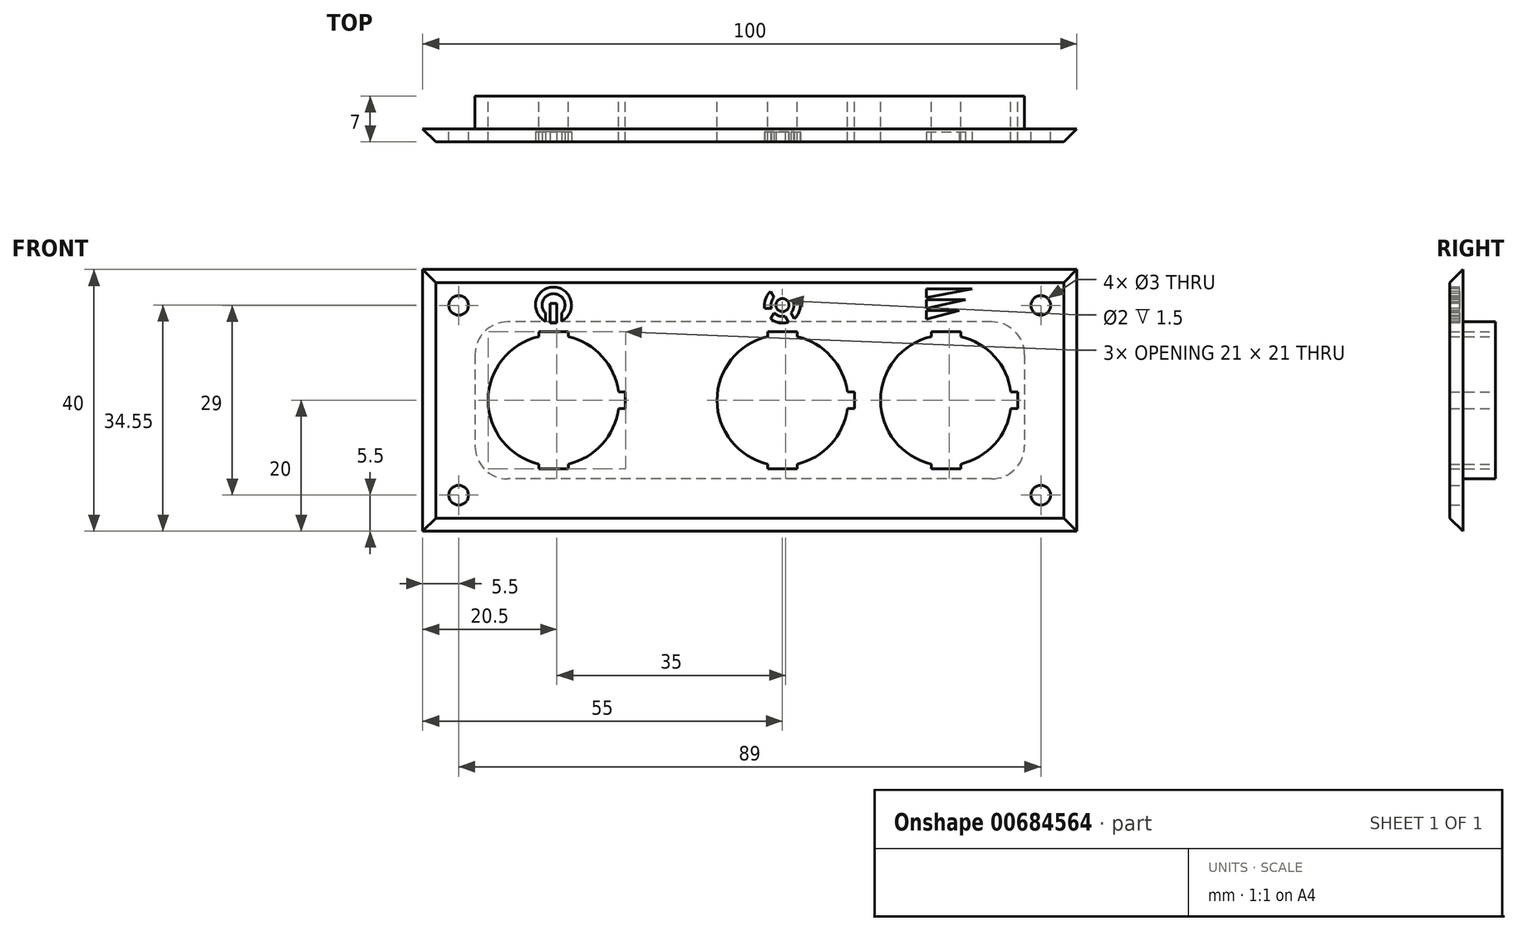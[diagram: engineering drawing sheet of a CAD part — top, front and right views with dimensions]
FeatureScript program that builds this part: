
annotation { "Feature Type Name" : "Feature", "Feature Type Description" : "" }
export const myFeature = defineFeature(function(context is Context, id is Id, definition is map)
    precondition{}
    {
        {
            var Q0;
            Q0=qCreatedBy(makeId("Front.planeOp"),FACE);
            var sketch = newSketch(context, id + "F0", { "sketchPlane" : qUnion([Q0])});
            skLineSegment(sketch, "E0.bottom", {"start": v(0, 0) * mm, "end": v(100, 0) * mm});
            skLineSegment(sketch, "E0.top", {"start": v(0, 40) * mm, "end": v(100, 40) * mm});
            skLineSegment(sketch, "E0.left", {"start": v(0, 0) * mm, "end": v(0, 40) * mm});
            skLineSegment(sketch, "E0.right", {"start": v(100, 0) * mm, "end": v(100, 40) * mm});
            skSolve(sketch);
        }
        {
            var Q0;
            Q0=makeQuery(id+"F0.imprint","IMPRINT",FACE,{"disambiguationData":[TD([[makeQuery(id+"F0.imprint","IMPRINT",EDGE,{"derivedFrom":sQuery(id+"F0.wireOp",EDGE,"E0.bottom")}),1.0]])]});
            extrude(context, id + "F1", {"entities" : qUnion([Q0]), "depth" : 2 * mm});
        }
        {
            var Q0;
            Q0=makeQuery(id+"F1.opExtrude","CAP_EDGE",EDGE,{"disambiguationData":[OSD([sQuery(id+"F0.wireOp",EDGE,"E0.right")])],"isStart":false});
            var Q1;
            Q1=makeQuery(id+"F1.opExtrude","CAP_EDGE",EDGE,{"disambiguationData":[OSD([sQuery(id+"F0.wireOp",EDGE,"E0.top")])],"isStart":false});
            var Q2;
            Q2=makeQuery(id+"F1.opExtrude","CAP_EDGE",EDGE,{"disambiguationData":[OSD([sQuery(id+"F0.wireOp",EDGE,"E0.bottom")])],"isStart":false});
            var Q3;
            Q3=makeQuery(id+"F1.opExtrude","CAP_EDGE",EDGE,{"disambiguationData":[OSD([sQuery(id+"F0.wireOp",EDGE,"E0.left")])],"isStart":false});
            chamfer(context, id + "F2", {"entities" : qUnion([Q0, Q1, Q2, Q3]), "width" : 2 * mm, "tangentPropagation" : true});
        }
        {
            var Q0;
            Q0=makeQuery(id+"F1.opExtrude","CAP_FACE",FACE,{"disambiguationData":[OSD([sQuery(id+"F0.wireOp",EDGE,"E0.bottom"),sQuery(id+"F0.wireOp",EDGE,"E0.top"),sQuery(id+"F0.wireOp",EDGE,"E0.left"),sQuery(id+"F0.wireOp",EDGE,"E0.right")])],"isStart":true});
            var sketch = newSketch(context, id + "F3", { "sketchPlane" : qUnion([Q0])});
            skLineSegment(sketch, "E1.bottom", {"start": v(-92, 32) * mm, "end": v(-8, 32) * mm});
            skLineSegment(sketch, "E1.top", {"start": v(-92, 8) * mm, "end": v(-8, 8) * mm});
            skLineSegment(sketch, "E1.left", {"start": v(-92, 32) * mm, "end": v(-92, 8) * mm});
            skLineSegment(sketch, "E1.right", {"start": v(-8, 32) * mm, "end": v(-8, 8) * mm});
            skSolve(sketch);
        }
        {
            var Q0;
            Q0=makeQuery(id+"F3.imprint","IMPRINT",FACE,{"disambiguationData":[TD([[makeQuery(id+"F3.imprint","IMPRINT",EDGE,{"derivedFrom":sQuery(id+"F3.wireOp",EDGE,"E1.bottom")}),-1.0]])]});
            extrude(context, id + "F4", {"entities" : qUnion([Q0]), "operationType" : NewBodyOperationType.ADD, "depth" : 5 * mm});
        }
        {
            var Q0;
            Q0=makeQuery(id+"F1.opExtrude","CAP_FACE",FACE,{"disambiguationData":[OSD([sQuery(id+"F0.wireOp",EDGE,"E0.bottom"),sQuery(id+"F0.wireOp",EDGE,"E0.top"),sQuery(id+"F0.wireOp",EDGE,"E0.left"),sQuery(id+"F0.wireOp",EDGE,"E0.right")])],"isStart":true});
            var sketch = newSketch(context, id + "F5", { "sketchPlane" : qUnion([Q0])});
            skCircle(sketch, "E2", {"center": v(-94.5, 34.5) * mm, "radius": 1.5 * mm});
            skCircle(sketch, "E3", {"center": v(-5.5, 34.5) * mm, "radius": 1.5 * mm});
            skCircle(sketch, "E4", {"center": v(-5.5, 5.5) * mm, "radius": 1.5 * mm});
            skCircle(sketch, "E5", {"center": v(-94.5, 5.5) * mm, "radius": 1.5 * mm});
            skSolve(sketch);
        }
        {
            var Q0;
            Q0=makeQuery(id+"F5.imprint","IMPRINT",FACE,{"disambiguationData":[TD([[makeQuery(id+"F5.imprint","IMPRINT",EDGE,{"derivedFrom":sQuery(id+"F5.wireOp",EDGE,"E2")}),1.0]])]});
            var Q1;
            Q1=makeQuery(id+"F5.imprint","IMPRINT",FACE,{"disambiguationData":[TD([[makeQuery(id+"F5.imprint","IMPRINT",EDGE,{"derivedFrom":sQuery(id+"F5.wireOp",EDGE,"E5")}),1.0]])]});
            var Q2;
            Q2=makeQuery(id+"F5.imprint","IMPRINT",FACE,{"disambiguationData":[TD([[makeQuery(id+"F5.imprint","IMPRINT",EDGE,{"derivedFrom":sQuery(id+"F5.wireOp",EDGE,"E3")}),1.0]])]});
            var Q3;
            Q3=makeQuery(id+"F5.imprint","IMPRINT",FACE,{"disambiguationData":[TD([[makeQuery(id+"F5.imprint","IMPRINT",EDGE,{"derivedFrom":sQuery(id+"F5.wireOp",EDGE,"E4")}),1.0]])]});
            extrude(context, id + "F6", {"entities" : qUnion([Q0, Q1, Q2, Q3]), "operationType" : NewBodyOperationType.REMOVE, "endBound" : BoundingType.THROUGH_ALL, "oppositeDirection" : true, "depth" : 25 * mm});
        }
        {
            var Q0;
            Q0=makeQuery(id+"F4.opExtrude","SWEPT_EDGE",EDGE,{"disambiguationData":[OSD([sQuery(id+"F3.wireOp",EDGE,"E1.top"),sQuery(id+"F3.wireOp",EDGE,"E1.left")])]});
            var Q1;
            Q1=makeQuery(id+"F4.opExtrude","SWEPT_EDGE",EDGE,{"disambiguationData":[OSD([sQuery(id+"F3.wireOp",EDGE,"E1.bottom"),sQuery(id+"F3.wireOp",EDGE,"E1.left")])]});
            var Q2;
            Q2=makeQuery(id+"F4.opExtrude","SWEPT_EDGE",EDGE,{"disambiguationData":[OSD([sQuery(id+"F3.wireOp",EDGE,"E1.top"),sQuery(id+"F3.wireOp",EDGE,"E1.right")])]});
            var Q3;
            Q3=makeQuery(id+"F4.opExtrude","SWEPT_EDGE",EDGE,{"disambiguationData":[OSD([sQuery(id+"F3.wireOp",EDGE,"E1.bottom"),sQuery(id+"F3.wireOp",EDGE,"E1.right")])]});
            fillet(context, id + "F7", {"entities" : qUnion([Q0, Q1, Q2, Q3]), "radius" : 5 * mm, "tangentPropagation" : true, "allowEdgeOverflow" : false});
        }
        {
            var Q0;
            Q0=makeQuery(id+"F4.opExtrude","CAP_FACE",FACE,{"disambiguationData":[OSD([sQuery(id+"F3.wireOp",EDGE,"E1.bottom"),sQuery(id+"F3.wireOp",EDGE,"E1.top"),sQuery(id+"F3.wireOp",EDGE,"E1.left"),sQuery(id+"F3.wireOp",EDGE,"E1.right")])],"isStart":false});
            var sketch = newSketch(context, id + "F8", { "sketchPlane" : qUnion([Q0])});
            skCircle(sketch, "E6", {"center": v(-80, 20) * mm, "radius": 10 * mm});
            skCircle(sketch, "E7", {"center": v(-55, 20) * mm, "radius": 10 * mm});
            skCircle(sketch, "E8", {"center": v(-20, 20) * mm, "radius": 10 * mm});
            skSolve(sketch);
        }
        {
            var Q0;
            Q0=makeQuery(id+"F8.imprint","IMPRINT",FACE,{"disambiguationData":[TD([[makeQuery(id+"F8.imprint","IMPRINT",EDGE,{"derivedFrom":sQuery(id+"F8.wireOp",EDGE,"E6")}),1.0]])]});
            var Q1;
            Q1=makeQuery(id+"F8.imprint","IMPRINT",FACE,{"disambiguationData":[TD([[makeQuery(id+"F8.imprint","IMPRINT",EDGE,{"derivedFrom":sQuery(id+"F8.wireOp",EDGE,"E7")}),1.0]])]});
            var Q2;
            Q2=makeQuery(id+"F8.imprint","IMPRINT",FACE,{"disambiguationData":[TD([[makeQuery(id+"F8.imprint","IMPRINT",EDGE,{"derivedFrom":sQuery(id+"F8.wireOp",EDGE,"E8")}),1.0]])]});
            extrude(context, id + "F9", {"entities" : qUnion([Q0, Q1, Q2]), "operationType" : NewBodyOperationType.REMOVE, "endBound" : BoundingType.THROUGH_ALL, "oppositeDirection" : true, "depth" : 25 * mm});
        }
        {
            var Q0;
            Q0=makeQuery(id+"F4.opExtrude","CAP_FACE",FACE,{"disambiguationData":[OSD([sQuery(id+"F3.wireOp",EDGE,"E1.bottom"),sQuery(id+"F3.wireOp",EDGE,"E1.top"),sQuery(id+"F3.wireOp",EDGE,"E1.left"),sQuery(id+"F3.wireOp",EDGE,"E1.right")])],"isStart":false});
            var sketch = newSketch(context, id + "F10", { "sketchPlane" : qUnion([Q0])});
            skLineSegment(sketch, "E9.bottom", {"start": v(-91, 21.25) * mm, "end": v(-85.88, 21.25) * mm});
            skLineSegment(sketch, "E9.top", {"start": v(-91, 18.75) * mm, "end": v(-85.88, 18.75) * mm});
            skLineSegment(sketch, "E9.left", {"start": v(-91, 21.25) * mm, "end": v(-91, 18.75) * mm});
            skLineSegment(sketch, "E9.right", {"start": v(-85.88, 21.25) * mm, "end": v(-85.88, 18.75) * mm});
            skLineSegment(sketch, "E10.bottom", {"start": v(-66, 21.25) * mm, "end": v(-50.9, 21.25) * mm});
            skLineSegment(sketch, "E10.top", {"start": v(-66, 18.75) * mm, "end": v(-50.9, 18.75) * mm});
            skLineSegment(sketch, "E10.left", {"start": v(-66, 21.25) * mm, "end": v(-66, 18.75) * mm});
            skLineSegment(sketch, "E10.right", {"start": v(-50.9, 21.25) * mm, "end": v(-50.9, 18.75) * mm});
            skLineSegment(sketch, "E11.bottom", {"start": v(-31, 21.25) * mm, "end": v(-25.22, 21.25) * mm});
            skLineSegment(sketch, "E11.top", {"start": v(-31, 18.75) * mm, "end": v(-25.22, 18.75) * mm});
            skLineSegment(sketch, "E11.left", {"start": v(-31, 21.25) * mm, "end": v(-31, 18.75) * mm});
            skLineSegment(sketch, "E11.right", {"start": v(-25.22, 21.25) * mm, "end": v(-25.22, 18.75) * mm});
            skSolve(sketch);
        }
        {
            var Q0;
            {var subQ0=sQuery(id+"F10.wireOp",EDGE,"E9.left");Q0=makeQuery(id+"F10.imprint","IMPRINT",FACE,{"disambiguationData":[TD([[makeQuery(id+"F10.imprint","IMPRINT",EDGE,{"derivedFrom":subQ0}),1.0]])]});}
            var Q1;
            {var subQ0=sQuery(id+"F10.wireOp",EDGE,"E10.left");Q1=makeQuery(id+"F10.imprint","IMPRINT",FACE,{"disambiguationData":[TD([[makeQuery(id+"F10.imprint","IMPRINT",EDGE,{"derivedFrom":subQ0}),1.0]])]});}
            var Q2;
            {var subQ0=sQuery(id+"F10.wireOp",EDGE,"E11.left");Q2=makeQuery(id+"F10.imprint","IMPRINT",FACE,{"disambiguationData":[TD([[makeQuery(id+"F10.imprint","IMPRINT",EDGE,{"derivedFrom":subQ0}),1.0]])]});}
            extrude(context, id + "F11", {"entities" : qUnion([Q0, Q1, Q2]), "operationType" : NewBodyOperationType.REMOVE, "endBound" : BoundingType.THROUGH_ALL, "oppositeDirection" : true, "depth" : 5 * mm});
        }
        {
            var Q0;
            Q0=makeQuery(id+"F4.opExtrude","CAP_FACE",FACE,{"disambiguationData":[OSD([sQuery(id+"F3.wireOp",EDGE,"E1.bottom"),sQuery(id+"F3.wireOp",EDGE,"E1.top"),sQuery(id+"F3.wireOp",EDGE,"E1.left"),sQuery(id+"F3.wireOp",EDGE,"E1.right")])],"isStart":false});
            var sketch = newSketch(context, id + "F12", { "sketchPlane" : qUnion([Q0])});
            skLineSegment(sketch, "E12.bottom", {"start": v(-82.25, 30.5) * mm, "end": v(-77.75, 30.5) * mm});
            skLineSegment(sketch, "E12.top", {"start": v(-82.25, 9.5) * mm, "end": v(-77.75, 9.5) * mm});
            skLineSegment(sketch, "E12.left", {"start": v(-82.25, 30.5) * mm, "end": v(-82.25, 9.5) * mm});
            skLineSegment(sketch, "E12.right", {"start": v(-77.75, 30.5) * mm, "end": v(-77.75, 9.5) * mm});
            skLineSegment(sketch, "E13.bottom", {"start": v(-57.25, 30.5) * mm, "end": v(-52.75, 30.5) * mm});
            skLineSegment(sketch, "E13.top", {"start": v(-57.25, 9.5) * mm, "end": v(-52.75, 9.5) * mm});
            skLineSegment(sketch, "E13.left", {"start": v(-57.25, 30.5) * mm, "end": v(-57.25, 9.5) * mm});
            skLineSegment(sketch, "E13.right", {"start": v(-52.75, 30.5) * mm, "end": v(-52.75, 9.5) * mm});
            skLineSegment(sketch, "E14.bottom", {"start": v(-22.25, 30.5) * mm, "end": v(-17.75, 30.5) * mm});
            skLineSegment(sketch, "E14.top", {"start": v(-22.25, 9.5) * mm, "end": v(-17.75, 9.5) * mm});
            skLineSegment(sketch, "E14.left", {"start": v(-22.25, 30.5) * mm, "end": v(-22.25, 9.5) * mm});
            skLineSegment(sketch, "E14.right", {"start": v(-17.75, 30.5) * mm, "end": v(-17.75, 9.5) * mm});
            skSolve(sketch);
        }
        {
            var Q0;
            {var subQ0=sQuery(id+"F12.wireOp",EDGE,"E12.bottom");Q0=makeQuery(id+"F12.imprint","IMPRINT",FACE,{"disambiguationData":[TD([[makeQuery(id+"F12.imprint","IMPRINT",EDGE,{"derivedFrom":subQ0}),-1.0]])]});}
            var Q1;
            {var subQ0=sQuery(id+"F12.wireOp",EDGE,"E12.top");Q1=makeQuery(id+"F12.imprint","IMPRINT",FACE,{"disambiguationData":[TD([[makeQuery(id+"F12.imprint","IMPRINT",EDGE,{"derivedFrom":subQ0}),1.0]])]});}
            var Q2;
            {var subQ0=sQuery(id+"F12.wireOp",EDGE,"E13.top");Q2=makeQuery(id+"F12.imprint","IMPRINT",FACE,{"disambiguationData":[TD([[makeQuery(id+"F12.imprint","IMPRINT",EDGE,{"derivedFrom":subQ0}),1.0]])]});}
            var Q3;
            {var subQ0=sQuery(id+"F12.wireOp",EDGE,"E13.bottom");Q3=makeQuery(id+"F12.imprint","IMPRINT",FACE,{"disambiguationData":[TD([[makeQuery(id+"F12.imprint","IMPRINT",EDGE,{"derivedFrom":subQ0}),-1.0]])]});}
            var Q4;
            {var subQ0=sQuery(id+"F12.wireOp",EDGE,"E14.bottom");Q4=makeQuery(id+"F12.imprint","IMPRINT",FACE,{"disambiguationData":[TD([[makeQuery(id+"F12.imprint","IMPRINT",EDGE,{"derivedFrom":subQ0}),-1.0]])]});}
            var Q5;
            {var subQ0=sQuery(id+"F12.wireOp",EDGE,"E14.top");Q5=makeQuery(id+"F12.imprint","IMPRINT",FACE,{"disambiguationData":[TD([[makeQuery(id+"F12.imprint","IMPRINT",EDGE,{"derivedFrom":subQ0}),1.0]])]});}
            extrude(context, id + "F13", {"entities" : qUnion([Q0, Q1, Q2, Q3, Q4, Q5]), "operationType" : NewBodyOperationType.REMOVE, "endBound" : BoundingType.THROUGH_ALL, "oppositeDirection" : true, "depth" : 5.5 * mm});
        }
        {
            var Q0;
            Q0=makeQuery(id+"F1.opExtrude","CAP_FACE",FACE,{"disambiguationData":[OSD([sQuery(id+"F0.wireOp",EDGE,"E0.bottom"),sQuery(id+"F0.wireOp",EDGE,"E0.top"),sQuery(id+"F0.wireOp",EDGE,"E0.left"),sQuery(id+"F0.wireOp",EDGE,"E0.right")])],"isStart":false});
            var sketch = newSketch(context, id + "F14", { "sketchPlane" : qUnion([Q0])});
            skLineSegment(sketch, "E15", {"start": v(2.8, 37.3) * mm, "end": v(102.8, 37.3) * mm, "construction": true});
            skLineSegment(sketch, "E16", {"start": v(3.28, 31.8) * mm, "end": v(103.18, 31.8) * mm, "construction": true});
            skLineSegment(sketch, "E17.bottom", {"start": v(19.5, 31.8) * mm, "end": v(20.5, 31.8) * mm});
            skLineSegment(sketch, "E17.top", {"start": v(19.5, 34.8) * mm, "end": v(20.5, 34.8) * mm});
            skLineSegment(sketch, "E17.left", {"start": v(19.5, 31.8) * mm, "end": v(19.5, 34.8) * mm});
            skLineSegment(sketch, "E17.right", {"start": v(20.5, 31.8) * mm, "end": v(20.5, 34.8) * mm});
            skCircle(sketch, "E18", {"center": v(20, 34.55) * mm, "radius": 2.75 * mm});
            skCircle(sketch, "E19", {"center": v(20, 34.55) * mm, "radius": 1.75 * mm});
            skLineSegment(sketch, "E20.bottom", {"start": v(18.75, 30.98) * mm, "end": v(21.25, 30.98) * mm});
            skLineSegment(sketch, "E20.top", {"start": v(18.75, 35.15) * mm, "end": v(21.25, 35.15) * mm});
            skLineSegment(sketch, "E20.left", {"start": v(18.75, 30.98) * mm, "end": v(18.75, 35.15) * mm});
            skLineSegment(sketch, "E20.right", {"start": v(21.25, 30.98) * mm, "end": v(21.25, 35.15) * mm});
            skSolve(sketch);
        }
        {
            var Q0;
            {var subQ0=sQuery(id+"F14.wireOp",EDGE,"E20.left");var subQ1=sQuery(id+"F14.wireOp",EDGE,"E18");var subQ2=makeQuery(id+"F14.imprint","INTERSECT",VERTEX,{"derivedFrom":[subQ1,subQ0]});Q0=makeQuery(id+"F14.imprint","IMPRINT",FACE,{"disambiguationData":[TD([[makeQuery(id+"F14.imprint","IMPRINT",EDGE,{"disambiguationData":[TD([[subQ2,1.0]])],"derivedFrom":subQ1}),1.0]])]});}
            var Q1;
            {var subQ0=sQuery(id+"F14.wireOp",EDGE,"E17.top");Q1=makeQuery(id+"F14.imprint","IMPRINT",FACE,{"disambiguationData":[TD([[makeQuery(id+"F14.imprint","IMPRINT",EDGE,{"derivedFrom":subQ0}),-1.0]])]});}
            var Q2;
            {var subQ0=sQuery(id+"F14.wireOp",EDGE,"E18");var subQ4=sQuery(id+"F14.wireOp",EDGE,"E17.left");var subQ5=makeQuery(id+"F14.imprint","INTERSECT",VERTEX,{"derivedFrom":[subQ4,subQ0]});Q2=makeQuery(id+"F14.imprint","IMPRINT",FACE,{"disambiguationData":[TD([[makeQuery(id+"F14.imprint","IMPRINT",EDGE,{"disambiguationData":[TD([[subQ5,-1.0]])],"derivedFrom":subQ4}),-1.0]])]});}
            extrude(context, id + "F15", {"entities" : qUnion([Q0, Q1, Q2]), "operationType" : NewBodyOperationType.REMOVE, "oppositeDirection" : true, "depth" : 1.5 * mm});
        }
        {
            var Q0;
            Q0=makeQuery(id+"F1.opExtrude","CAP_FACE",FACE,{"disambiguationData":[OSD([sQuery(id+"F0.wireOp",EDGE,"E0.bottom"),sQuery(id+"F0.wireOp",EDGE,"E0.top"),sQuery(id+"F0.wireOp",EDGE,"E0.left"),sQuery(id+"F0.wireOp",EDGE,"E0.right")])],"isStart":false});
            var sketch = newSketch(context, id + "F16", { "sketchPlane" : qUnion([Q0])});
            skCircle(sketch, "E21", {"center": v(55, 34.55) * mm, "radius": 2.75 * mm});
            skCircle(sketch, "E22", {"center": v(55, 34.55) * mm, "radius": 1.75 * mm});
            skCircle(sketch, "E23", {"center": v(55, 34.55) * mm, "radius": 1 * mm});
            skLineSegment(sketch, "E24", {"start": v(52.48, 39.57) * mm, "end": v(52.72, 39.7) * mm});
            skLineSegment(sketch, "E25", {"start": v(57.31, 38.74) * mm, "end": v(57.38, 38.7) * mm});
            skLineSegment(sketch, "E26.bottom", {"start": v(51, 35.05) * mm, "end": v(59, 35.05) * mm});
            skLineSegment(sketch, "E26.top", {"start": v(51, 34.05) * mm, "end": v(59, 34.05) * mm});
            skLineSegment(sketch, "E26.left", {"start": v(51, 35.05) * mm, "end": v(51, 34.05) * mm});
            skLineSegment(sketch, "E26.right", {"start": v(59, 35.05) * mm, "end": v(59, 34.05) * mm});
            skLineSegment(sketch, "E27", {"start": v(52.57, 37.76) * mm, "end": v(56.57, 30.84) * mm});
            skLineSegment(sketch, "E28", {"start": v(56.57, 30.84) * mm, "end": v(57.43, 31.34) * mm});
            skLineSegment(sketch, "E29", {"start": v(57.43, 31.34) * mm, "end": v(53.54, 38.07) * mm});
            skLineSegment(sketch, "E30", {"start": v(53.54, 38.07) * mm, "end": v(52.57, 37.76) * mm});
            skLineSegment(sketch, "E31", {"start": v(52.4, 31.04) * mm, "end": v(56.41, 38) * mm});
            skLineSegment(sketch, "E32", {"start": v(56.41, 38) * mm, "end": v(57.28, 37.5) * mm});
            skLineSegment(sketch, "E33", {"start": v(57.28, 37.5) * mm, "end": v(53.05, 30.18) * mm});
            skLineSegment(sketch, "E34", {"start": v(53.05, 30.18) * mm, "end": v(52.4, 31.04) * mm});
            skSolve(sketch);
        }
        {
            var Q0;
            {var subQ0=sQuery(id+"F16.wireOp",EDGE,"E26.top");var subQ3=sQuery(id+"F16.wireOp",EDGE,"E27");var subQ5=makeQuery(id+"F16.imprint","INTERSECT",VERTEX,{"derivedFrom":[subQ0,subQ3]});Q0=makeQuery(id+"F16.imprint","IMPRINT",FACE,{"disambiguationData":[TD([[makeQuery(id+"F16.imprint","IMPRINT",EDGE,{"disambiguationData":[TD([[subQ5,1.0]])],"derivedFrom":subQ0}),-1.0]])]});}
            var Q1;
            {var subQ0=sQuery(id+"F16.wireOp",EDGE,"E27");var subQ1=sQuery(id+"F16.wireOp",EDGE,"E26.top");var subQ2=makeQuery(id+"F16.imprint","INTERSECT",VERTEX,{"derivedFrom":[subQ1,subQ0]});Q1=makeQuery(id+"F16.imprint","IMPRINT",FACE,{"disambiguationData":[TD([[makeQuery(id+"F16.imprint","IMPRINT",EDGE,{"disambiguationData":[TD([[subQ2,1.0]])],"derivedFrom":subQ0}),-1.0]])]});}
            var Q2;
            {var subQ0=sQuery(id+"F16.wireOp",EDGE,"E27");var subQ3=sQuery(id+"F16.wireOp",EDGE,"E31");var subQ5=makeQuery(id+"F16.imprint","INTERSECT",VERTEX,{"derivedFrom":[subQ0,subQ3]});Q2=makeQuery(id+"F16.imprint","IMPRINT",FACE,{"disambiguationData":[TD([[makeQuery(id+"F16.imprint","IMPRINT",EDGE,{"disambiguationData":[TD([[subQ5,1.0]])],"derivedFrom":subQ0}),-1.0]])]});}
            var Q3;
            {var subQ0=sQuery(id+"F16.wireOp",EDGE,"E31");var subQ1=sQuery(id+"F16.wireOp",EDGE,"E26.bottom");var subQ2=makeQuery(id+"F16.imprint","INTERSECT",VERTEX,{"derivedFrom":[subQ1,subQ0]});Q3=makeQuery(id+"F16.imprint","IMPRINT",FACE,{"disambiguationData":[TD([[makeQuery(id+"F16.imprint","IMPRINT",EDGE,{"disambiguationData":[TD([[subQ2,1.0]])],"derivedFrom":subQ0}),1.0]])]});}
            var Q4;
            {var subQ0=sQuery(id+"F16.wireOp",EDGE,"E31");var subQ3=sQuery(id+"F16.wireOp",EDGE,"E26.bottom");var subQ5=makeQuery(id+"F16.imprint","INTERSECT",VERTEX,{"derivedFrom":[subQ3,subQ0]});Q4=makeQuery(id+"F16.imprint","IMPRINT",FACE,{"disambiguationData":[TD([[makeQuery(id+"F16.imprint","IMPRINT",EDGE,{"disambiguationData":[TD([[subQ5,1.0]])],"derivedFrom":subQ3}),1.0]])]});}
            var Q5;
            {var subQ0=sQuery(id+"F16.wireOp",EDGE,"E31");var subQ1=sQuery(id+"F16.wireOp",EDGE,"E26.bottom");var subQ2=makeQuery(id+"F16.imprint","INTERSECT",VERTEX,{"derivedFrom":[subQ1,subQ0]});Q5=makeQuery(id+"F16.imprint","IMPRINT",FACE,{"disambiguationData":[TD([[makeQuery(id+"F16.imprint","IMPRINT",EDGE,{"disambiguationData":[TD([[subQ2,-1.0]])],"derivedFrom":subQ1}),1.0]])]});}
            var Q6;
            {var subQ5=sQuery(id+"F16.wireOp",EDGE,"E31");var subQ7=sQuery(id+"F16.wireOp",EDGE,"E26.bottom");var subQ8=makeQuery(id+"F16.imprint","INTERSECT",VERTEX,{"derivedFrom":[subQ7,subQ5]});Q6=makeQuery(id+"F16.imprint","IMPRINT",FACE,{"disambiguationData":[TD([[makeQuery(id+"F16.imprint","IMPRINT",EDGE,{"disambiguationData":[TD([[subQ8,-1.0]])],"derivedFrom":subQ7}),-1.0]])]});}
            var Q7;
            {var subQ0=sQuery(id+"F16.wireOp",EDGE,"E27");var subQ1=sQuery(id+"F16.wireOp",EDGE,"E26.top");var subQ2=makeQuery(id+"F16.imprint","INTERSECT",VERTEX,{"derivedFrom":[subQ1,subQ0]});Q7=makeQuery(id+"F16.imprint","IMPRINT",FACE,{"disambiguationData":[TD([[makeQuery(id+"F16.imprint","IMPRINT",EDGE,{"disambiguationData":[TD([[subQ2,-1.0]])],"derivedFrom":subQ1}),-1.0]])]});}
            var Q8;
            {var subQ0=sQuery(id+"F16.wireOp",EDGE,"E33");var subQ3=sQuery(id+"F16.wireOp",EDGE,"E26.top");var subQ5=makeQuery(id+"F16.imprint","INTERSECT",VERTEX,{"derivedFrom":[subQ3,subQ0]});Q8=makeQuery(id+"F16.imprint","IMPRINT",FACE,{"disambiguationData":[TD([[makeQuery(id+"F16.imprint","IMPRINT",EDGE,{"disambiguationData":[TD([[subQ5,-1.0]])],"derivedFrom":subQ3}),-1.0]])]});}
            var Q9;
            {var subQ0=sQuery(id+"F16.wireOp",EDGE,"E33");var subQ3=sQuery(id+"F16.wireOp",EDGE,"E29");var subQ5=makeQuery(id+"F16.imprint","INTERSECT",VERTEX,{"derivedFrom":[subQ3,subQ0]});Q9=makeQuery(id+"F16.imprint","IMPRINT",FACE,{"disambiguationData":[TD([[makeQuery(id+"F16.imprint","IMPRINT",EDGE,{"disambiguationData":[TD([[subQ5,1.0]])],"derivedFrom":subQ3}),-1.0]])]});}
            var Q10;
            {var subQ0=sQuery(id+"F16.wireOp",EDGE,"E29");var subQ1=sQuery(id+"F16.wireOp",EDGE,"E26.bottom");var subQ2=makeQuery(id+"F16.imprint","INTERSECT",VERTEX,{"derivedFrom":[subQ1,subQ0]});Q10=makeQuery(id+"F16.imprint","IMPRINT",FACE,{"disambiguationData":[TD([[makeQuery(id+"F16.imprint","IMPRINT",EDGE,{"disambiguationData":[TD([[subQ2,1.0]])],"derivedFrom":subQ0}),-1.0]])]});}
            var Q11;
            {var subQ0=sQuery(id+"F16.wireOp",EDGE,"E29");var subQ3=sQuery(id+"F16.wireOp",EDGE,"E26.bottom");var subQ5=makeQuery(id+"F16.imprint","INTERSECT",VERTEX,{"derivedFrom":[subQ3,subQ0]});Q11=makeQuery(id+"F16.imprint","IMPRINT",FACE,{"disambiguationData":[TD([[makeQuery(id+"F16.imprint","IMPRINT",EDGE,{"disambiguationData":[TD([[subQ5,-1.0]])],"derivedFrom":subQ3}),1.0]])]});}
            var Q12;
            {var subQ0=sQuery(id+"F16.wireOp",EDGE,"E33");var subQ1=sQuery(id+"F16.wireOp",EDGE,"E26.top");var subQ2=makeQuery(id+"F16.imprint","INTERSECT",VERTEX,{"derivedFrom":[subQ1,subQ0]});Q12=makeQuery(id+"F16.imprint","IMPRINT",FACE,{"disambiguationData":[TD([[makeQuery(id+"F16.imprint","IMPRINT",EDGE,{"disambiguationData":[TD([[subQ2,1.0]])],"derivedFrom":subQ0}),1.0]])]});}
            var Q13;
            {var subQ0=sQuery(id+"F16.wireOp",EDGE,"E31");var subQ1=sQuery(id+"F16.wireOp",EDGE,"E21");var subQ2=makeQuery(id+"F16.imprint","INTERSECT",VERTEX,{"disambiguationData":[OD(1.0)],"derivedFrom":[subQ1,subQ0]});Q13=makeQuery(id+"F16.imprint","IMPRINT",FACE,{"disambiguationData":[TD([[makeQuery(id+"F16.imprint","IMPRINT",EDGE,{"disambiguationData":[TD([[subQ2,-1.0]])],"derivedFrom":subQ1}),1.0]])]});}
            var Q14;
            {var subQ0=sQuery(id+"F16.wireOp",EDGE,"E27");var subQ1=sQuery(id+"F16.wireOp",EDGE,"E21");var subQ2=makeQuery(id+"F16.imprint","INTERSECT",VERTEX,{"disambiguationData":[OD(1.0)],"derivedFrom":[subQ1,subQ0]});Q14=makeQuery(id+"F16.imprint","IMPRINT",FACE,{"disambiguationData":[TD([[makeQuery(id+"F16.imprint","IMPRINT",EDGE,{"disambiguationData":[TD([[subQ2,-1.0]])],"derivedFrom":subQ1}),1.0]])]});}
            var Q15;
            {var subQ0=sQuery(id+"F16.wireOp",EDGE,"E26.bottom");var subQ1=sQuery(id+"F16.wireOp",EDGE,"E21");var subQ2=makeQuery(id+"F16.imprint","INTERSECT",VERTEX,{"disambiguationData":[OD(0.0)],"derivedFrom":[subQ1,subQ0]});Q15=makeQuery(id+"F16.imprint","IMPRINT",FACE,{"disambiguationData":[TD([[makeQuery(id+"F16.imprint","IMPRINT",EDGE,{"disambiguationData":[TD([[subQ2,1.0]])],"derivedFrom":subQ1}),1.0]])]});}
            var Q16;
            {var subQ0=sQuery(id+"F16.wireOp",EDGE,"E33");var subQ1=sQuery(id+"F16.wireOp",EDGE,"E21");var subQ2=makeQuery(id+"F16.imprint","INTERSECT",VERTEX,{"disambiguationData":[OD(0.0)],"derivedFrom":[subQ1,subQ0]});Q16=makeQuery(id+"F16.imprint","IMPRINT",FACE,{"disambiguationData":[TD([[makeQuery(id+"F16.imprint","IMPRINT",EDGE,{"disambiguationData":[TD([[subQ2,-1.0]])],"derivedFrom":subQ1}),1.0]])]});}
            var Q17;
            {var subQ0=sQuery(id+"F16.wireOp",EDGE,"E29");var subQ1=sQuery(id+"F16.wireOp",EDGE,"E21");var subQ2=makeQuery(id+"F16.imprint","INTERSECT",VERTEX,{"disambiguationData":[OD(0.0)],"derivedFrom":[subQ1,subQ0]});Q17=makeQuery(id+"F16.imprint","IMPRINT",FACE,{"disambiguationData":[TD([[makeQuery(id+"F16.imprint","IMPRINT",EDGE,{"disambiguationData":[TD([[subQ2,-1.0]])],"derivedFrom":subQ1}),1.0]])]});}
            var Q18;
            {var subQ0=sQuery(id+"F16.wireOp",EDGE,"E26.bottom");var subQ1=sQuery(id+"F16.wireOp",EDGE,"E21");var subQ2=makeQuery(id+"F16.imprint","INTERSECT",VERTEX,{"disambiguationData":[OD(1.0)],"derivedFrom":[subQ1,subQ0]});Q18=makeQuery(id+"F16.imprint","IMPRINT",FACE,{"disambiguationData":[TD([[makeQuery(id+"F16.imprint","IMPRINT",EDGE,{"disambiguationData":[TD([[subQ2,-1.0]])],"derivedFrom":subQ1}),1.0]])]});}
            extrude(context, id + "F17", {"entities" : qUnion([Q0, Q1, Q2, Q3, Q4, Q5, Q6, Q7, Q8, Q9, Q10, Q11, Q12, Q13, Q14, Q15, Q16, Q17, Q18]), "operationType" : NewBodyOperationType.REMOVE, "oppositeDirection" : true, "depth" : 1.5 * mm});
        }
        {
            var Q0;
            Q0=makeQuery(id+"F1.opExtrude","CAP_FACE",FACE,{"disambiguationData":[OSD([sQuery(id+"F0.wireOp",EDGE,"E0.bottom"),sQuery(id+"F0.wireOp",EDGE,"E0.top"),sQuery(id+"F0.wireOp",EDGE,"E0.left"),sQuery(id+"F0.wireOp",EDGE,"E0.right")])],"isStart":false});
            var sketch = newSketch(context, id + "F18", { "sketchPlane" : qUnion([Q0])});
            skLineSegment(sketch, "E35", {"start": v(84, 37) * mm, "end": v(77, 37) * mm});
            skLineSegment(sketch, "E36", {"start": v(77, 37) * mm, "end": v(77, 35.7) * mm});
            skLineSegment(sketch, "E37", {"start": v(77, 35.7) * mm, "end": v(84, 37) * mm});
            skLineSegment(sketch, "E38", {"start": v(77, 35.35) * mm, "end": v(83, 35.35) * mm});
            skLineSegment(sketch, "E39", {"start": v(83, 35.35) * mm, "end": v(77, 34.05) * mm});
            skLineSegment(sketch, "E40", {"start": v(77, 34.05) * mm, "end": v(77, 35.35) * mm});
            skLineSegment(sketch, "E41", {"start": v(82, 33.7) * mm, "end": v(77, 33.7) * mm});
            skLineSegment(sketch, "E42", {"start": v(77, 33.7) * mm, "end": v(77, 32.4) * mm});
            skLineSegment(sketch, "E43", {"start": v(77, 32.4) * mm, "end": v(82, 33.7) * mm});
            skSolve(sketch);
        }
        {
            var Q0;
            Q0=makeQuery(id+"F18.imprint","IMPRINT",FACE,{"disambiguationData":[TD([[makeQuery(id+"F18.imprint","IMPRINT",EDGE,{"derivedFrom":sQuery(id+"F18.wireOp",EDGE,"E35")}),1.0]])]});
            var Q1;
            Q1=makeQuery(id+"F18.imprint","IMPRINT",FACE,{"disambiguationData":[TD([[makeQuery(id+"F18.imprint","IMPRINT",EDGE,{"derivedFrom":sQuery(id+"F18.wireOp",EDGE,"E38")}),-1.0]])]});
            var Q2;
            Q2=makeQuery(id+"F18.imprint","IMPRINT",FACE,{"disambiguationData":[TD([[makeQuery(id+"F18.imprint","IMPRINT",EDGE,{"derivedFrom":sQuery(id+"F18.wireOp",EDGE,"E41")}),1.0]])]});
            extrude(context, id + "F19", {"entities" : qUnion([Q0, Q1, Q2]), "operationType" : NewBodyOperationType.REMOVE, "oppositeDirection" : true, "depth" : 1.5 * mm});
        }
    });
